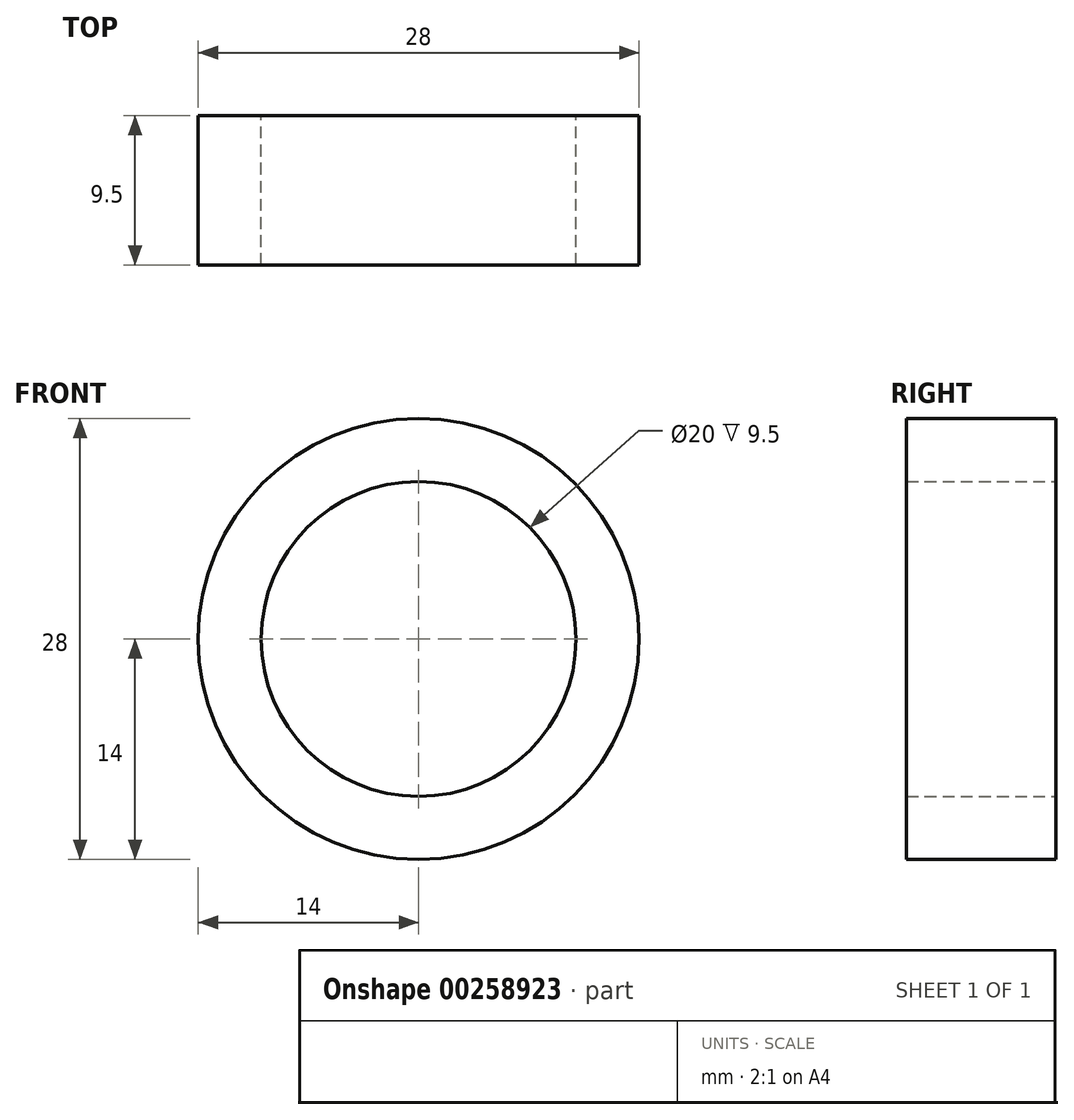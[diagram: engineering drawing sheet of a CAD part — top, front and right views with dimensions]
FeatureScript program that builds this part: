
annotation { "Feature Type Name" : "Feature", "Feature Type Description" : "" }
export const myFeature = defineFeature(function(context is Context, id is Id, definition is map)
    precondition{}
    {
        {
            var Q0;
            Q0=qCreatedBy(makeId("Front.planeOp"),FACE);
            var sketch = newSketch(context, id + "F0", { "sketchPlane" : qUnion([Q0])});
            skCircle(sketch, "E0", {"center": v(0, 0) * mm, "radius": 14 * mm});
            skCircle(sketch, "E1", {"center": v(0, 0) * mm, "radius": 10 * mm});
            skSolve(sketch);
        }
        {
            var Q0;
            Q0=makeQuery(id+"F0.imprint","IMPRINT",FACE,{"disambiguationData":[TD([[makeQuery(id+"F0.imprint","IMPRINT",EDGE,{"derivedFrom":sQuery(id+"F0.wireOp",EDGE,"E0")}),1.0]])]});
            extrude(context, id + "F1", {"entities" : qUnion([Q0]), "depth" : 9.5 * mm});
        }
    });
